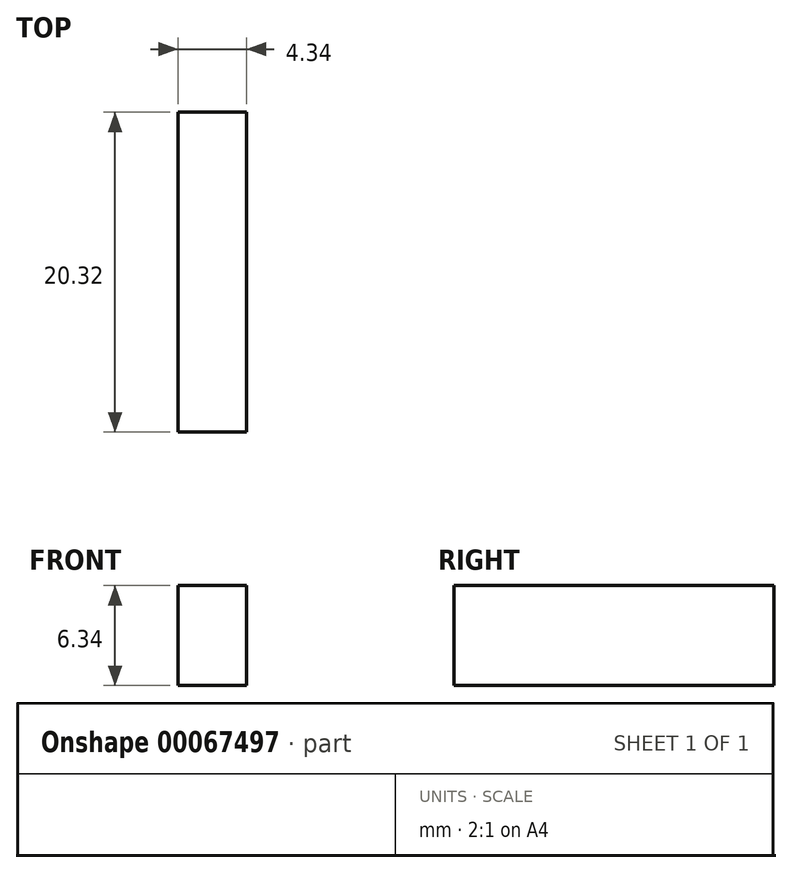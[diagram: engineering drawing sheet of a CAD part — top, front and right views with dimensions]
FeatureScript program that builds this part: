
annotation { "Feature Type Name" : "Feature", "Feature Type Description" : "" }
export const myFeature = defineFeature(function(context is Context, id is Id, definition is map)
    precondition{}
    {
        {
            var Q0;
            Q0=qCreatedBy(makeId("Right.planeOp"),FACE);
            var sketch = newSketch(context, id + "F0", { "sketchPlane" : qUnion([Q0])});
            skLineSegment(sketch, "E0.bottom", {"start": v(10.16, -3.17) * mm, "end": v(-10.16, -3.18) * mm});
            skLineSegment(sketch, "E0.top", {"start": v(10.16, 3.18) * mm, "end": v(-10.16, 3.18) * mm});
            skLineSegment(sketch, "E0.left", {"start": v(10.16, -3.18) * mm, "end": v(10.16, 3.18) * mm});
            skLineSegment(sketch, "E0.right", {"start": v(-10.16, -3.18) * mm, "end": v(-10.16, 3.17) * mm});
            skPoint(sketch, "E0.middle", {"position": v(0, 0) * mm});
            skSolve(sketch);
        }
        {
            var Q0;
            Q0 = qSketchRegion(id + "F0", true);
            extrude(context, id + "F1", {"entities" : qUnion([Q0]), "depth" : 4.34 * mm});
        }
    });
